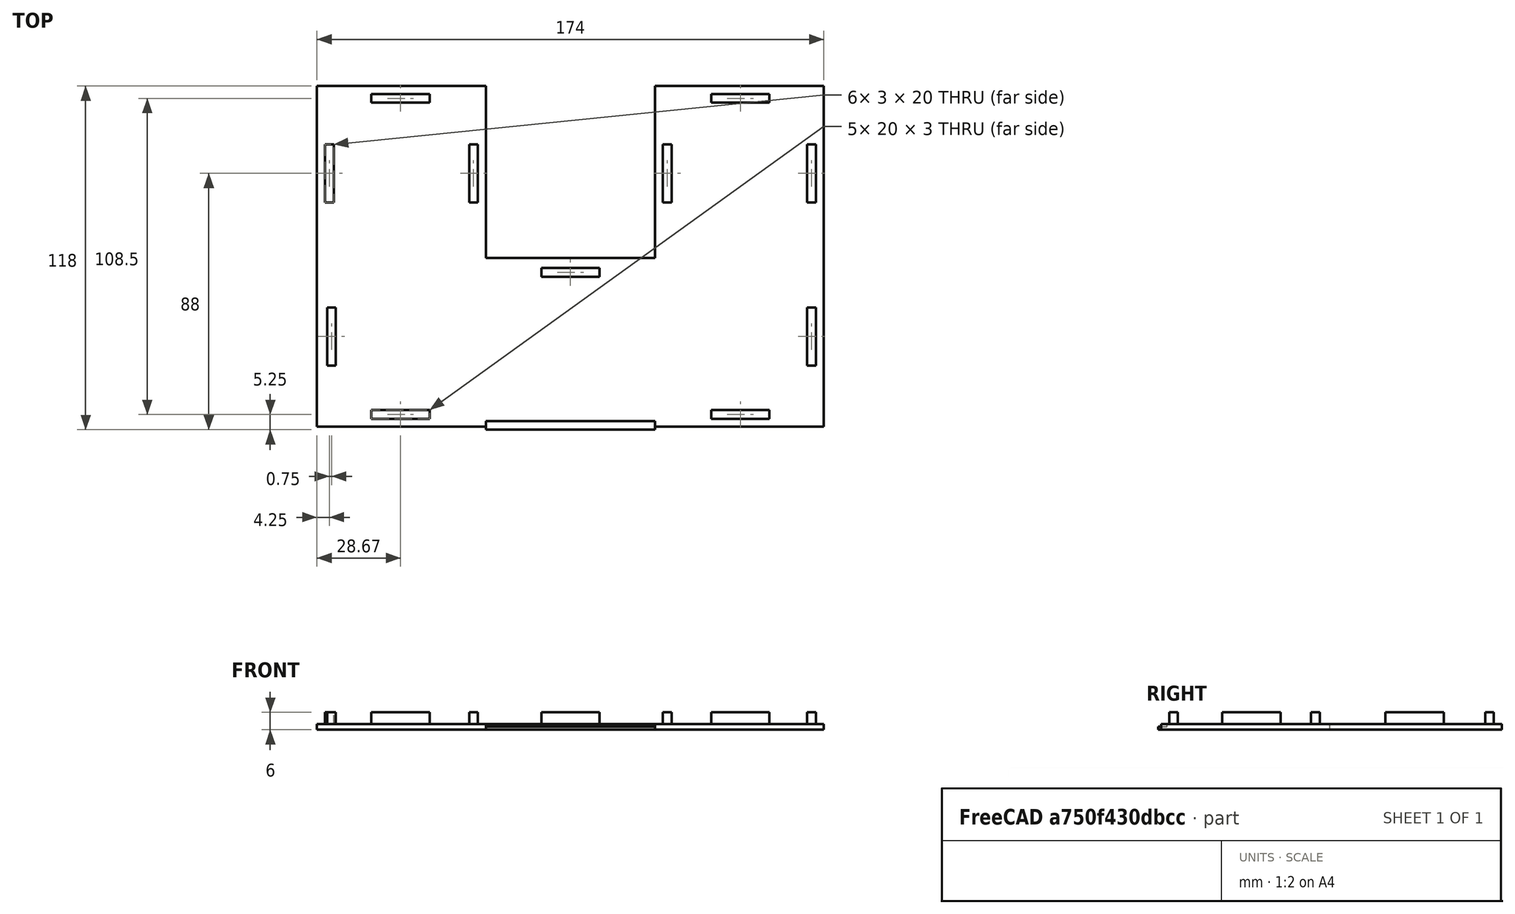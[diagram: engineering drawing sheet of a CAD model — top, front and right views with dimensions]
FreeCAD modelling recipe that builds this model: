
FCSTD DOCUMENT  (FreeCAD 0.21R33694 (Git))
Label: maze_cover_C_v3
License: All rights reserved
LicenseURL: https://en.wikipedia.org/wiki/All_rights_reserved
objects: Part::Box×15, Part::MultiFuse×1
note: 16 computed .brp shape members not serialized (recipe doc carries the construction recipe); baked Part::Feature solids carry a one-line shape summary decoded from their .brp

FEATURE [Part::Box] Box  label="Cube"
  AttacherType = Attacher::AttachEngine3D
  Height = 2
  Length = 58
  Placement = pos=(58,2,0) rot=(0,0,1;0rad)
  Width = 56
FEATURE [Part::Box] Box001  label="Cube001"
  AttacherType = Attacher::AttachEngine3D
  Height = 2
  Length = 58
  Width = 117
FEATURE [Part::Box] Box002  label="Cube002"
  AttacherType = Attacher::AttachEngine3D
  Height = 2
  Length = 58
  Placement = pos=(116,0,0) rot=(0,0,1;0rad)
  Width = 117
FEATURE [Part::Box] Box003  label="Cube003"
  AttacherType = Attacher::AttachEngine3D
  Height = 6
  Length = 20
  Placement = pos=(18.67,111.25,0) rot=(0,0,1;0rad)
  Width = 3
FEATURE [Part::Box] Box004  label="Cube004"
  AttacherType = Attacher::AttachEngine3D
  Height = 6
  Length = 20
  Placement = pos=(18.67,2.75,0) rot=(0,0,1;0rad)
  Width = 3
FEATURE [Part::Box] Box005  label="Cube005"
  AttacherType = Attacher::AttachEngine3D
  Height = 6
  Length = 20
  Placement = pos=(135.333,2.75,0) rot=(0,0,1;0rad)
  Width = 3
FEATURE [Part::Box] Box006  label="Cube006"
  AttacherType = Attacher::AttachEngine3D
  Height = 6
  Length = 20
  Placement = pos=(135.333,111.25,0) rot=(0,0,1;0rad)
  Width = 3
FEATURE [Part::Box] Box007  label="Cube007"
  AttacherType = Attacher::AttachEngine3D
  Height = 6
  Length = 20
  Placement = pos=(118.75,97,0) rot=(0,0,-1;1.5708rad)
  Width = 3
FEATURE [Part::Box] Box008  label="Cube008"
  AttacherType = Attacher::AttachEngine3D
  Height = 6
  Length = 20
  Placement = pos=(168.25,41,0) rot=(0,0,-1;1.5708rad)
  Width = 3
FEATURE [Part::Box] Box009  label="Cube009"
  AttacherType = Attacher::AttachEngine3D
  Height = 6
  Length = 20
  Placement = pos=(168.25,97,0) rot=(0,0,-1;1.5708rad)
  Width = 3
FEATURE [Part::Box] Box010  label="Cube010"
  AttacherType = Attacher::AttachEngine3D
  Height = 6
  Length = 20
  Placement = pos=(52.25,97,0) rot=(0,0,-1;1.5708rad)
  Width = 3
FEATURE [Part::Box] Box011  label="Cube011"
  AttacherType = Attacher::AttachEngine3D
  Height = 6
  Length = 20
  Placement = pos=(2.75,97,0) rot=(0,0,-1;1.5708rad)
  Width = 3
  expr: .Placement.Base.x = 2.75 mm
FEATURE [Part::Box] Box012  label="Cube012"
  AttacherType = Attacher::AttachEngine3D
  Height = 6
  Length = 20
  Placement = pos=(3.5,41,0) rot=(0,0,-1;1.5708rad)
  Width = 3
FEATURE [Part::Box] Box013  label="Cube013"
  AttacherType = Attacher::AttachEngine3D
  Height = 6
  Length = 20
  Placement = pos=(77,51.5,0) rot=(0,0,1;0rad)
  Width = 3
FEATURE [Part::Box] Box014  label="Cube014"
  AttacherType = Attacher::AttachEngine3D
  Height = 1
  Length = 58
  Placement = pos=(58,-1,0) rot=(0,0,1;0rad)
  Width = 3
FEATURE [Part::MultiFuse] Fusion
  Shapes = -> [Box014,Box013,Box012,Box011,Box010,Box009,Box008,Box007,Box006,Box005,Box004,Box003,Box002,Box001,Box]
